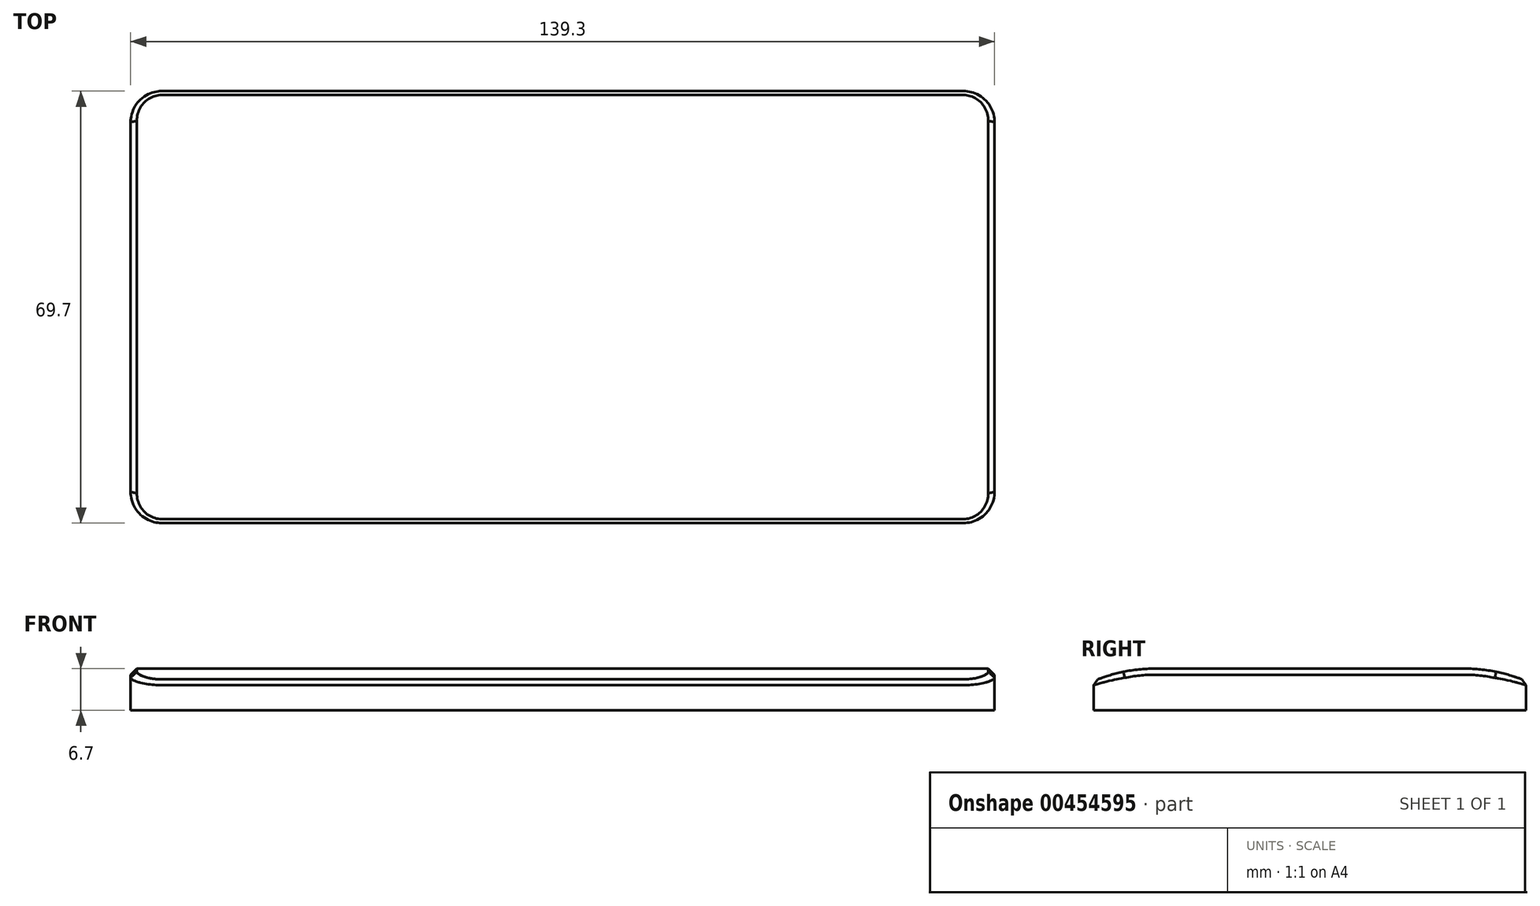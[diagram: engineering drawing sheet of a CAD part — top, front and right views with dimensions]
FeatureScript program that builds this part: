
annotation { "Feature Type Name" : "Feature", "Feature Type Description" : "" }
export const myFeature = defineFeature(function(context is Context, id is Id, definition is map)
    precondition{}
    {
        {
            var Q0;
            Q0=qCreatedBy(makeId("Top.planeOp"),FACE);
            var sketch = newSketch(context, id + "F0", { "sketchPlane" : qUnion([Q0])});
            skLineSegment(sketch, "E0.bottom", {"start": v(0, 0) * mm, "end": v(139.3, 0) * mm});
            skLineSegment(sketch, "E0.top", {"start": v(0, 69.7) * mm, "end": v(139.3, 69.7) * mm});
            skLineSegment(sketch, "E0.left", {"start": v(0, 0) * mm, "end": v(0, 69.7) * mm});
            skLineSegment(sketch, "E0.right", {"start": v(139.3, 0) * mm, "end": v(139.3, 69.7) * mm});
            skSolve(sketch);
        }
        {
            var Q0;
            Q0=makeQuery(id+"F0.imprint","IMPRINT",FACE,{"disambiguationData":[TD([[makeQuery(id+"F0.imprint","IMPRINT",EDGE,{"derivedFrom":sQuery(id+"F0.wireOp",EDGE,"E0.bottom")}),1.0]])]});
            extrude(context, id + "F1", {"entities" : qUnion([Q0]), "depth" : 6.7 * mm});
        }
        {
            var Q0;
            Q0=makeQuery(id+"F1.opExtrude","SWEPT_EDGE",EDGE,{"disambiguationData":[OSD([sQuery(id+"F0.wireOp",EDGE,"E0.bottom"),sQuery(id+"F0.wireOp",EDGE,"E0.right")])]});
            var Q1;
            Q1=makeQuery(id+"F1.opExtrude","SWEPT_EDGE",EDGE,{"disambiguationData":[OSD([sQuery(id+"F0.wireOp",EDGE,"E0.top"),sQuery(id+"F0.wireOp",EDGE,"E0.right")])]});
            var Q2;
            Q2=makeQuery(id+"F1.opExtrude","SWEPT_EDGE",EDGE,{"disambiguationData":[OSD([sQuery(id+"F0.wireOp",EDGE,"E0.top"),sQuery(id+"F0.wireOp",EDGE,"E0.left")])]});
            var Q3;
            Q3=makeQuery(id+"F1.opExtrude","SWEPT_EDGE",EDGE,{"disambiguationData":[OSD([sQuery(id+"F0.wireOp",EDGE,"E0.bottom"),sQuery(id+"F0.wireOp",EDGE,"E0.left")])]});
            fillet(context, id + "F2", {"entities" : qUnion([Q0, Q1, Q2, Q3]), "radius" : 5 * mm, "tangentPropagation" : true, "allowEdgeOverflow" : false});
        }
        {
            var Q0;
            Q0=qCreatedBy(makeId("Right.planeOp"),FACE);
            var sketch = newSketch(context, id + "F3", { "sketchPlane" : qUnion([Q0])});
            skArc(sketch, "E1", {"start": v(9.85, 6.7) * mm, "mid": v(4.82, 6.2) * mm, "end": v(0, 4.7) * mm});
            skLineSegment(sketch, "E2", {"start": v(34.85, 0) * mm, "end": v(34.85, 6.7) * mm, "construction": true});
            skLineSegment(sketch, "E3", {"start": v(34.85, 6.7) * mm, "end": v(9.85, 6.7) * mm});
            skLineSegment(sketch, "E4", {"start": v(0, 4.7) * mm, "end": v(-5, 4.7) * mm});
            skLineSegment(sketch, "E5", {"start": v(-5, 4.7) * mm, "end": v(-5, 11.7) * mm});
            skLineSegment(sketch, "E6", {"start": v(-5, 11.7) * mm, "end": v(34.85, 11.7) * mm});
            skLineSegment(sketch, "E7.MirrorCS", {"start": v(34.85, 6.7) * mm, "end": v(59.85, 6.7) * mm});
            skLineSegment(sketch, "E8.MirrorCS", {"start": v(74.7, 11.7) * mm, "end": v(34.85, 11.7) * mm});
            skArc(sketch, "E9.MirrorCS", {"start": v(59.85, 6.7) * mm, "mid": v(64.88, 6.2) * mm, "end": v(69.7, 4.7) * mm});
            skLineSegment(sketch, "E10.MirrorCS", {"start": v(74.7, 4.7) * mm, "end": v(74.7, 11.7) * mm});
            skLineSegment(sketch, "E11.MirrorCS", {"start": v(69.7, 4.7) * mm, "end": v(74.7, 4.7) * mm});
            skSolve(sketch);
        }
        {
            var Q0;
            Q0=makeQuery(id+"F3.imprint","IMPRINT",FACE,{"disambiguationData":[TD([[makeQuery(id+"F3.imprint","IMPRINT",EDGE,{"derivedFrom":sQuery(id+"F3.wireOp",EDGE,"E1")}),-1.0]])]});
            extrude(context, id + "F4", {"entities" : qUnion([Q0]), "operationType" : NewBodyOperationType.REMOVE, "depth" : 160 * mm});
        }
        {
            var Q0;
            Q0=makeQuery(id+"F1.opExtrude","CAP_EDGE",EDGE,{"disambiguationData":[OSD([sQuery(id+"F0.wireOp",EDGE,"E0.left")])],"isStart":false});
            chamfer(context, id + "F5", {"entities" : qUnion([Q0]), "width" : 1 * mm, "tangentPropagation" : true});
        }
    });
